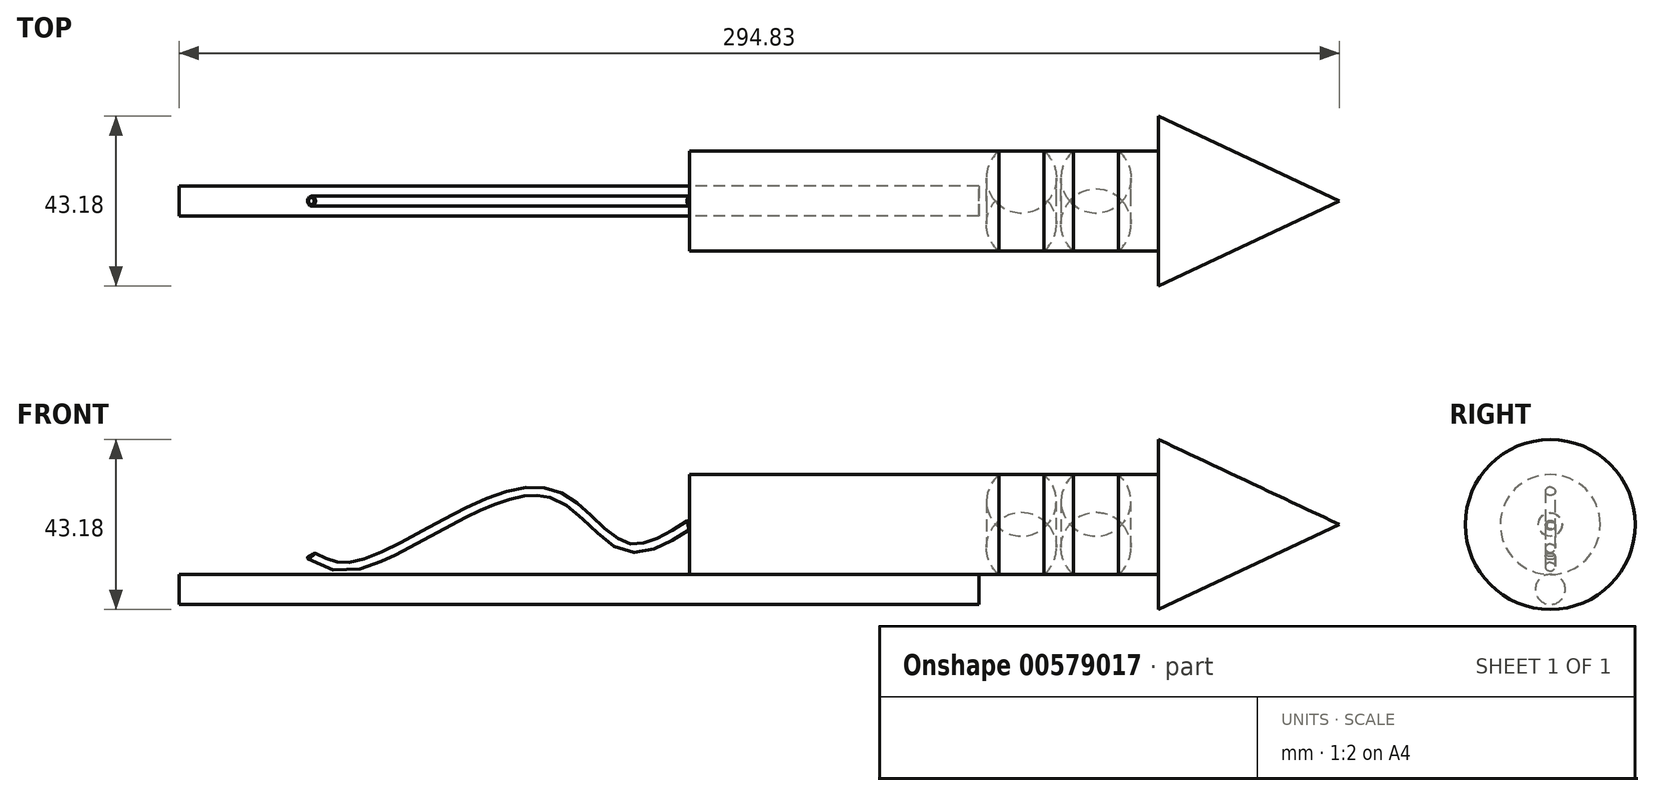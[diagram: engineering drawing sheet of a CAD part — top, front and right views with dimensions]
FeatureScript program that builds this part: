
annotation { "Feature Type Name" : "Feature", "Feature Type Description" : "" }
export const myFeature = defineFeature(function(context is Context, id is Id, definition is map)
    precondition{}
    {
        {
            var Q0;
            Q0=qCreatedBy(makeId("Front.planeOp"),FACE);
            var sketch = newSketch(context, id + "F0", { "sketchPlane" : qUnion([Q0])});
            skLineSegment(sketch, "E0", {"start": v(-67.5, 30.9) * mm, "end": v(-67.5, 34.71) * mm});
            skLineSegment(sketch, "E1", {"start": v(-67.5, 30.9) * mm, "end": v(135.7, 30.9) * mm});
            skLineSegment(sketch, "E2", {"start": v(135.7, 30.9) * mm, "end": v(135.7, 34.71) * mm});
            skLineSegment(sketch, "E3", {"start": v(135.7, 34.71) * mm, "end": v(-67.5, 34.71) * mm});
            skLineSegment(sketch, "E4", {"start": v(0, 0) * mm, "end": v(0, 30.9) * mm, "construction": true});
            skSolve(sketch);
        }
        {
            var Q0;
            Q0=makeQuery(id+"F0.imprint","IMPRINT",FACE,{"disambiguationData":[TD([[makeQuery(id+"F0.imprint","IMPRINT",EDGE,{"derivedFrom":sQuery(id+"F0.wireOp",EDGE,"E0")}),-1.0]])]});
            var sketch = newSketch(context, id + "F1", { "sketchPlane" : qUnion([Q0])});
            skLineSegment(sketch, "E5", {"start": v(62.22, 25.82) * mm, "end": v(227.32, 25.82) * mm});
            skLineSegment(sketch, "E6", {"start": v(227.32, 47.41) * mm, "end": v(181.34, 25.82) * mm});
            skLineSegment(sketch, "E7", {"start": v(62.22, 34.71) * mm, "end": v(181.34, 34.71) * mm});
            skLineSegment(sketch, "E8", {"start": v(181.34, 25.82) * mm, "end": v(181.34, 47.41) * mm});
            skLineSegment(sketch, "E9", {"start": v(62.22, 25.82) * mm, "end": v(62.22, 47.41) * mm});
            skLineSegment(sketch, "E10", {"start": v(227.32, 47.41) * mm, "end": v(227.32, 25.82) * mm});
            skLineSegment(sketch, "E11", {"start": v(62.22, 47.41) * mm, "end": v(227.32, 47.41) * mm});
            skSolve(sketch);
        }
        {
            var Q0;
            Q0=makeQuery(id+"F0.imprint","IMPRINT",FACE,{"disambiguationData":[TD([[makeQuery(id+"F0.imprint","IMPRINT",EDGE,{"derivedFrom":sQuery(id+"F0.wireOp",EDGE,"E0")}),-1.0]])]});
            var Q1;
            Q1=sQuery(id+"F0.wireOp",EDGE,"E1");
            revolve(context, id + "F2", {"entities" : qUnion([Q0]), "axis" : qUnion([Q1]), "revolveType" : RevolveType.FULL});
        }
        {
            var Q0;
            {var subQ0=sQuery(id+"F1.wireOp",EDGE,"E6");Q0=makeQuery(id+"F1.imprint","IMPRINT",FACE,{"disambiguationData":[TD([[makeQuery(id+"F1.imprint","IMPRINT",EDGE,{"derivedFrom":subQ0}),-1.0]])]});}
            var Q1;
            {var subQ0=sQuery(id+"F1.wireOp",EDGE,"E8");var subQ1=sQuery(id+"F1.wireOp",EDGE,"E7");var subQ2=makeQuery(id+"F1.imprint","INTERSECT",VERTEX,{"derivedFrom":[subQ1,subQ0]});Q1=makeQuery(id+"F1.imprint","IMPRINT",FACE,{"disambiguationData":[TD([[makeQuery(id+"F1.imprint","IMPRINT",EDGE,{"disambiguationData":[TD([[subQ2,1.0]])],"derivedFrom":subQ1}),1.0]])]});}
            var Q2;
            Q2=sQuery(id+"F1.wireOp",EDGE,"E11");
            revolve(context, id + "F3", {"entities" : qUnion([Q0, Q1]), "axis" : qUnion([Q2]), "revolveType" : RevolveType.FULL});
        }
        {
            var Q0;
            Q0=makeQuery(id+"F3.opRevolve","SWEPT_FACE",FACE,{"disambiguationData":[OSD([sQuery(id+"F1.wireOp",EDGE,"E9")])]});
            var sketch = newSketch(context, id + "F4", { "sketchPlane" : qUnion([Q0])});
            skCircle(sketch, "E12", {"center": v(0, 47.41) * mm, "radius": 1.27 * mm});
            skSolve(sketch);
        }
        {
            var Q0;
            Q0=qCreatedBy(makeId("Front.planeOp"),FACE);
            var sketch = newSketch(context, id + "F5", { "sketchPlane" : qUnion([Q0])});
            skPoint(sketch, "E13.0", {"position": v(62.22, 47.41) * mm});
            skFitSpline(sketch, "E14", {"points": [v(62.22, 47.41) * mm, v(45.9, 41.77) * mm, v(29.41, 54.38) * mm, v(6.33, 50.88) * mm, v(-23.73, 36.82) * mm, v(-34.11, 39.54) * mm], "startDerivative": vector(-91.79, -58.69) * mm, "endDerivative": vector(-62.17, 34.07) * mm});
            skSolve(sketch);
        }
        {
            var Q0;
            Q0=makeQuery(id+"F4.imprint","IMPRINT",FACE,{"disambiguationData":[TD([[makeQuery(id+"F4.imprint","IMPRINT",EDGE,{"derivedFrom":sQuery(id+"F4.wireOp",EDGE,"E12")}),1.0]])]});
            var Q1;
            Q1=sQuery(id+"F5.wireOp",EDGE,"E14");
            sweep(context, id + "F6", {"profiles" : qUnion([Q0]), "path" : qUnion([Q1])});
        }
        {
            var Q0;
            Q0=qCreatedBy(makeId("Front.planeOp"),FACE);
            var sketch = newSketch(context, id + "F7", { "sketchPlane" : qUnion([Q0])});
            skLineSegment(sketch, "E15.0", {"start": v(62.22, 47.41) * mm, "end": v(227.32, 47.41) * mm});
            skLineSegment(sketch, "E15.1", {"start": v(62.22, 34.71) * mm, "end": v(181.34, 34.71) * mm});
            skArc(sketch, "E16", {"start": v(140.83, 34.71) * mm, "mid": v(146.54, 32.63) * mm, "end": v(152.26, 34.71) * mm});
            skArc(sketch, "E17", {"start": v(159.77, 34.71) * mm, "mid": v(165.49, 32.63) * mm, "end": v(171.2, 34.71) * mm});
            skSolve(sketch);
        }
        {
            var Q0;
            Q0 = qSketchRegion(id + "F7", true);
            var Q1;
            Q1=sQuery(id+"F7.wireOp",EDGE,"E15.0");
            revolve(context, id + "F8", {"entities" : qUnion([Q0]), "axis" : qUnion([Q1]), "revolveType" : RevolveType.FULL});
        }
        {
            var Q0;
            Q0=makeQuery(id+"F6.opSweep","CAP_EDGE",EDGE,{"disambiguationData":[OSD([sQuery(id+"F4.wireOp",EDGE,"E12"),sQuery(id+"F5.wireOp",VERTEX,"E14.end")])],"isStart":false});
            var Q1;
            Q1=makeQuery(id+"F6.opSweep","CAP_EDGE",EDGE,{"disambiguationData":[OSD([sQuery(id+"F4.wireOp",EDGE,"E12"),sQuery(id+"F5.wireOp",VERTEX,"E14.start")])],"isStart":true});
            fillet(context, id + "F9", {"entities" : qUnion([Q0, Q1]), "radius" : 0.38 * mm, "tangentPropagation" : true, "allowEdgeOverflow" : false});
        }
    });
